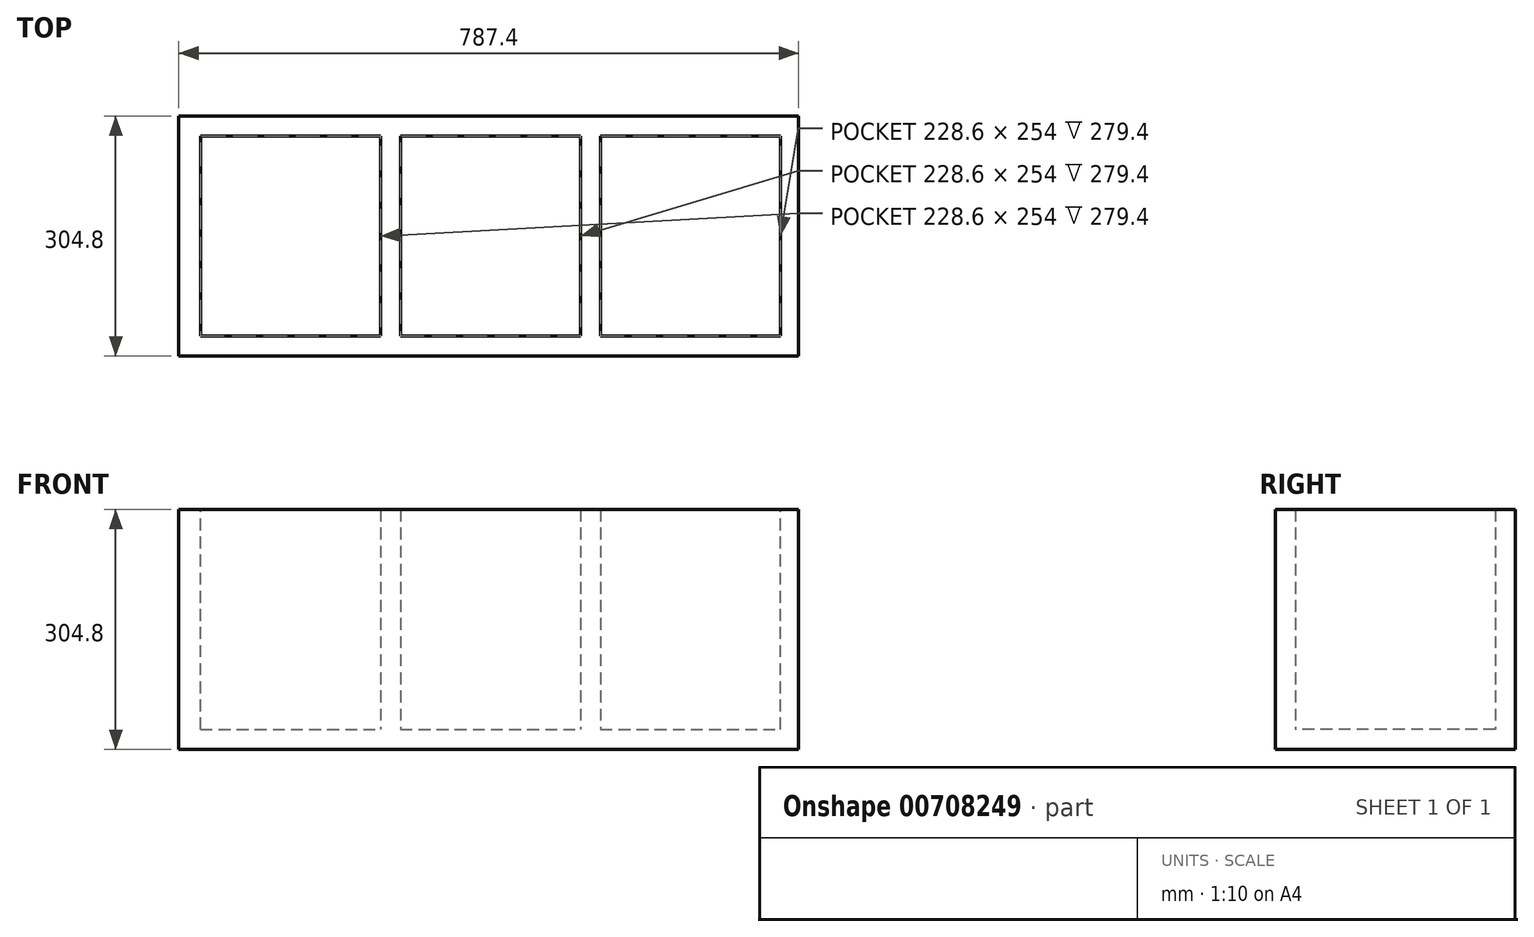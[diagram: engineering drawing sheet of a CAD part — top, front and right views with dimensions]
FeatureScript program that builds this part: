
annotation { "Feature Type Name" : "Feature", "Feature Type Description" : "" }
export const myFeature = defineFeature(function(context is Context, id is Id, definition is map)
    precondition{}
    {
        {
            var Q0;
            Q0=qCreatedBy(makeId("Top.planeOp"),FACE);
            var sketch = newSketch(context, id + "F0", { "sketchPlane" : qUnion([Q0])});
            skLineSegment(sketch, "E0.bottom", {"start": v(0, 0) * mm, "end": v(-787.4, 0) * mm});
            skLineSegment(sketch, "E0.top", {"start": v(0, 304.8) * mm, "end": v(-787.4, 304.8) * mm});
            skLineSegment(sketch, "E0.left", {"start": v(0, 0) * mm, "end": v(0, 304.8) * mm});
            skLineSegment(sketch, "E0.right", {"start": v(-787.4, 0) * mm, "end": v(-787.4, 304.8) * mm});
            skSolve(sketch);
        }
        {
            var Q0;
            Q0=makeQuery(id+"F0.imprint","IMPRINT",FACE,{"disambiguationData":[TD([[makeQuery(id+"F0.imprint","IMPRINT",EDGE,{"derivedFrom":sQuery(id+"F0.wireOp",EDGE,"E0.bottom")}),-1.0]])]});
            extrude(context, id + "F1", {"entities" : qUnion([Q0]), "depth" : 304.8 * mm, "offsetDistance" : 25.4 * mm});
        }
        {
            var Q0;
            Q0=makeQuery(id+"F1.opExtrude","CAP_FACE",FACE,{"disambiguationData":[OSD([sQuery(id+"F0.wireOp",EDGE,"E0.bottom"),sQuery(id+"F0.wireOp",EDGE,"E0.top"),sQuery(id+"F0.wireOp",EDGE,"E0.left"),sQuery(id+"F0.wireOp",EDGE,"E0.right")])],"isStart":false});
            var sketch = newSketch(context, id + "F2", { "sketchPlane" : qUnion([Q0])});
            skLineSegment(sketch, "E1", {"start": v(-787.4, 257.8) * mm, "end": v(-762, 257.8) * mm});
            skLineSegment(sketch, "E2", {"start": v(-759.88, 304.8) * mm, "end": v(-759.88, 279.4) * mm});
            skLineSegment(sketch, "E3.bottom", {"start": v(-759.88, 279.4) * mm, "end": v(-23.28, 279.4) * mm});
            skLineSegment(sketch, "E3.top", {"start": v(-759.88, 25.4) * mm, "end": v(-23.28, 25.4) * mm});
            skLineSegment(sketch, "E3.left", {"start": v(-759.88, 279.4) * mm, "end": v(-759.88, 25.4) * mm});
            skLineSegment(sketch, "E3.right", {"start": v(-23.28, 279.4) * mm, "end": v(-23.28, 25.4) * mm});
            skLineSegment(sketch, "E4.bottom", {"start": v(-759.88, 279.4) * mm, "end": v(-531.28, 279.4) * mm});
            skLineSegment(sketch, "E4.top", {"start": v(-759.88, 25.4) * mm, "end": v(-531.28, 25.4) * mm});
            skLineSegment(sketch, "E4.right", {"start": v(-531.28, 279.4) * mm, "end": v(-531.28, 25.4) * mm});
            skSolve(sketch);
        }
        {
            var Q0;
            Q0=makeQuery(id+"F2.imprint","IMPRINT",FACE,{"disambiguationData":[TD([[makeQuery(id+"F2.imprint","IMPRINT",EDGE,{"derivedFrom":sQuery(id+"F2.wireOp",EDGE,"E3.bottom")}),-1.0]])]});
            var sketch = newSketch(context, id + "F3", { "sketchPlane" : qUnion([Q0])});
            skSolve(sketch);
        }
        {
            var Q0;
            Q0=makeQuery(id+"F2.imprint","IMPRINT",FACE,{"disambiguationData":[TD([[makeQuery(id+"F2.imprint","IMPRINT",EDGE,{"derivedFrom":sQuery(id+"F2.wireOp",EDGE,"E4.bottom")}),-1.0]])]});
            var Q1;
            Q1=makeQuery(id+"F2.imprint","IMPRINT",FACE,{"disambiguationData":[TD([[makeQuery(id+"F2.imprint","IMPRINT",EDGE,{"derivedFrom":sQuery(id+"F2.wireOp",EDGE,"E3.bottom")}),-1.0]])]});
            extrude(context, id + "F4", {"entities" : qUnion([Q0, Q1]), "operationType" : NewBodyOperationType.REMOVE, "oppositeDirection" : true, "depth" : 279.4 * mm, "offsetDistance" : 25.4 * mm});
        }
        {
            var Q0;
            Q0=makeQuery(id+"F3.imprint","IMPRINT",FACE,{"disambiguationData":[TD([[makeQuery(id+"F3.imprint","IMPRINT",EDGE,{"derivedFrom":makeQuery(id+"F2.imprint","IMPRINT",EDGE,{"derivedFrom":sQuery(id+"F2.wireOp",EDGE,"E3.bottom")})}),-1.0]])]});
            extrude(context, id + "F5", {"entities" : qUnion([Q0]), "operationType" : NewBodyOperationType.REMOVE, "oppositeDirection" : true, "depth" : 279.4 * mm, "offsetDistance" : 25.4 * mm});
        }
        {
            var Q0;
            Q0=makeQuery(id+"F4.boolean.opBoolean","COPY",FACE,{"derivedFrom":makeQuery(id+"F4.opExtrude","CAP_FACE",FACE,{"disambiguationData":[OSD([sQuery(id+"F2.wireOp",EDGE,"E3.bottom"),sQuery(id+"F2.wireOp",EDGE,"E3.top"),sQuery(id+"F2.wireOp",EDGE,"E3.right"),sQuery(id+"F2.wireOp",EDGE,"E4.bottom"),sQuery(id+"F2.wireOp",EDGE,"E4.top"),sQuery(id+"F2.wireOp",EDGE,"E3.left")])],"isStart":false})});
            var sketch = newSketch(context, id + "F6", { "sketchPlane" : qUnion([Q0])});
            skLineSegment(sketch, "E5.bottom", {"start": v(-531.28, 279.4) * mm, "end": v(-505.88, 279.4) * mm});
            skLineSegment(sketch, "E5.top", {"start": v(-531.28, 25.4) * mm, "end": v(-505.88, 25.4) * mm});
            skLineSegment(sketch, "E5.left", {"start": v(-531.28, 279.4) * mm, "end": v(-531.28, 25.4) * mm});
            skLineSegment(sketch, "E5.right", {"start": v(-505.88, 279.4) * mm, "end": v(-505.88, 25.4) * mm});
            skSolve(sketch);
        }
        {
            var Q0;
            Q0=makeQuery(id+"F6.imprint","IMPRINT",FACE,{"disambiguationData":[TD([[makeQuery(id+"F6.imprint","IMPRINT",EDGE,{"derivedFrom":sQuery(id+"F6.wireOp",EDGE,"E5.bottom")}),-1.0]])]});
            var Q1;
            Q1=makeQuery(id+"F1.opExtrude","CAP_FACE",FACE,{"disambiguationData":[OSD([sQuery(id+"F0.wireOp",EDGE,"E0.bottom"),sQuery(id+"F0.wireOp",EDGE,"E0.top"),sQuery(id+"F0.wireOp",EDGE,"E0.left"),sQuery(id+"F0.wireOp",EDGE,"E0.right")])],"isStart":false});
            extrude(context, id + "F7", {"entities" : qUnion([Q0]), "operationType" : NewBodyOperationType.ADD, "endBound" : BoundingType.UP_TO_SURFACE, "depth" : 25.4 * mm, "endBoundEntityFace" : qUnion([Q1]), "offsetDistance" : 25.4 * mm});
        }
        {
            var Q0;
            {var subQ0=sQuery(id+"F2.wireOp",EDGE,"E4.bottom");var subQ1=sQuery(id+"F2.wireOp",EDGE,"E3.bottom");var subQ2=sQuery(id+"F2.wireOp",EDGE,"E4.top");var subQ3=sQuery(id+"F2.wireOp",EDGE,"E3.top");var subQ4=sQuery(id+"F2.wireOp",EDGE,"E3.right");Q0=makeQuery(id+"F7.boolean.opBoolean","SPLIT",FACE,{"disambiguationData":[TD([makeQuery(id+"F4.boolean.opBoolean","COPY",FACE,{"derivedFrom":makeQuery(id+"F4.opExtrude","SWEPT_FACE",FACE,{"disambiguationData":[OSD([subQ4])]})})])],"derivedFrom":makeQuery(id+"F4.boolean.opBoolean","COPY",FACE,{"derivedFrom":makeQuery(id+"F4.opExtrude","CAP_FACE",FACE,{"disambiguationData":[OSD([subQ1,subQ3,subQ4,subQ0,subQ2,sQuery(id+"F2.wireOp",EDGE,"E3.left")])],"isStart":false})})});}
            var sketch = newSketch(context, id + "F8", { "sketchPlane" : qUnion([Q0])});
            skLineSegment(sketch, "E6.bottom", {"start": v(-277.28, 279.4) * mm, "end": v(-251.88, 279.4) * mm});
            skLineSegment(sketch, "E6.top", {"start": v(-277.28, 25.4) * mm, "end": v(-251.88, 25.4) * mm});
            skLineSegment(sketch, "E6.left", {"start": v(-277.28, 279.4) * mm, "end": v(-277.28, 25.4) * mm});
            skLineSegment(sketch, "E6.right", {"start": v(-251.88, 279.4) * mm, "end": v(-251.88, 25.4) * mm});
            skSolve(sketch);
        }
        {
            var Q0;
            Q0=makeQuery(id+"F8.imprint","IMPRINT",FACE,{"disambiguationData":[TD([[makeQuery(id+"F8.imprint","IMPRINT",EDGE,{"derivedFrom":sQuery(id+"F8.wireOp",EDGE,"E6.bottom")}),-1.0]])]});
            var Q1;
            {var subQ0=sQuery(id+"F0.wireOp",EDGE,"E0.right");var subQ1=sQuery(id+"F0.wireOp",EDGE,"E0.left");var subQ2=sQuery(id+"F0.wireOp",EDGE,"E0.top");var subQ3=sQuery(id+"F0.wireOp",EDGE,"E0.bottom");Q1=makeQuery(id+"F7.boolean.opBoolean","MERGE",FACE,{"derivedFrom":[makeQuery(id+"F1.opExtrude","CAP_FACE",FACE,{"disambiguationData":[OSD([subQ3,subQ2,subQ1,subQ0])],"isStart":false}),makeQuery(id+"F7.opExtrude","CAP_FACE",FACE,{"disambiguationData":[OSD([subQ3,subQ2,subQ1,subQ0])],"isStart":false})]});}
            extrude(context, id + "F9", {"entities" : qUnion([Q0]), "operationType" : NewBodyOperationType.ADD, "endBound" : BoundingType.UP_TO_SURFACE, "depth" : 279.4 * mm, "endBoundEntityFace" : qUnion([Q1]), "offsetDistance" : 25.4 * mm});
        }
    });
